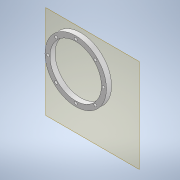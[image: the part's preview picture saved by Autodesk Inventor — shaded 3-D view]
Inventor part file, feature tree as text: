
AUTODESK INVENTOR PART (.ipt)
format: ipt  version: 2022 (Build 260153000, 153)  size: 142,336 bytes
history: native  units: in
note: dims shown in document units (in); Inventor stores cm internally (conversion verified against a paired STEP export)
features: other x4, reference x3, plane x1, extrude x1, sketch x1
ambient origin geometry x8: Origin, YZ Plane, XZ Plane, XY Plane, X Axis, Y Axis, Z Axis, Center Point
bodies: Solid1 (feature_tree)
feature tree (10):
  plane  "Work Plane1"
  extrude  "Extrusion1"  Depth=0.2992in TaperAngle=0.0deg
  sketch  "Sketch1"  dims[d0=0.0079in d1=0.2992in d2=0.0in]
  reference  "Reference1"
  reference  "Reference2"
  reference  "Reference3"
  other  "<userpath>\Documents\CAD\guardSwerve1\Assembly1.iam"
  other  "Assembly1.iam"
  other  "lower_plate:1"
  other  "Undercarriage:1"
